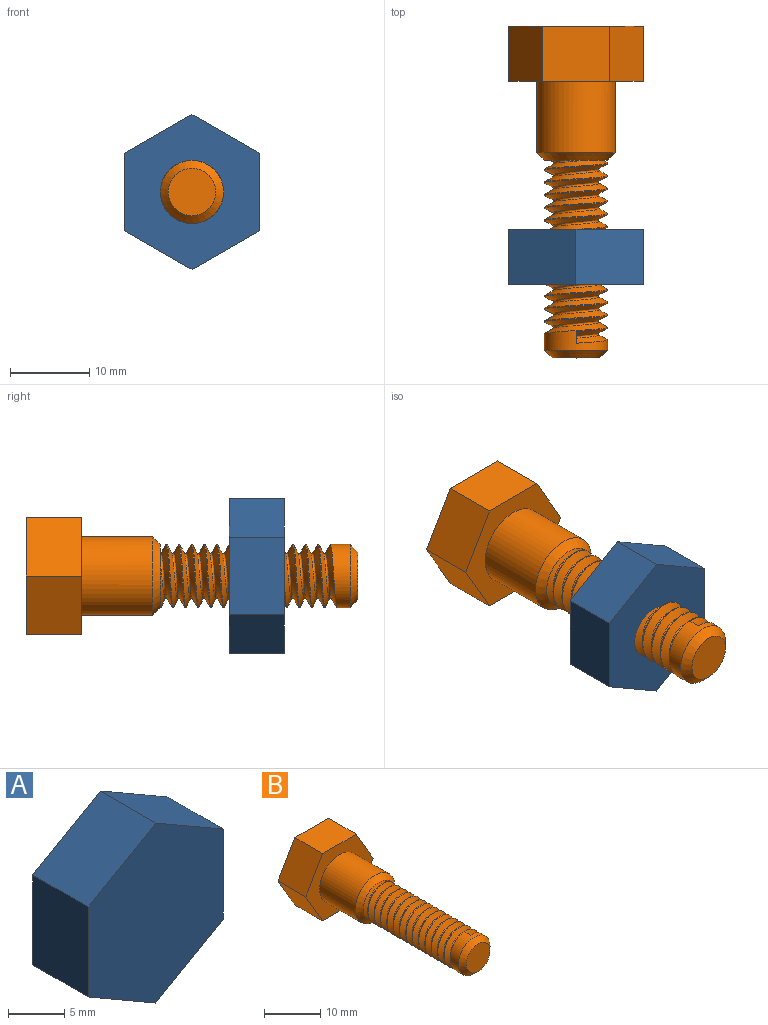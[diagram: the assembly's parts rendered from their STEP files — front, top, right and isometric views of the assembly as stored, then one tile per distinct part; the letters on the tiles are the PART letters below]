
ASSEMBLY  parts=2 mates=1
PART A: 8 faces, bbox 17x7x19.6 mm
  f0: plane 9.82x7mm, normal (1,0,0), area 68.7mm2, adj f1,f5,f6,f7
  f1: plane 8.5x7mm, normal (0.5,0,0.87), area 68.7mm2, adj f0,f2,f6,f7
  f2: plane 8.5x7mm, normal (-0.5,0,0.87), area 68.7mm2, adj f1,f3,f6,f7
  f3: plane 9.82x7mm, normal (-1,0,0), area 68.7mm2, adj f2,f4,f6,f7
  f4: plane 8.5x7mm, normal (-0.5,0,-0.87), area 68.7mm2, adj f3,f5,f6,f7
  f5: plane 8.5x7mm, normal (0.5,0,-0.87), area 68.7mm2, adj f0,f4,f6,f7
  f6: plane 19.63x17mm, normal (0,-1,0), area 250.3mm2, adj f0,f1,f2,f3,f4,f5
  f7: plane 19.63x17mm, normal (0,1,0), area 250.3mm2, adj f0,f1,f2,f3,f4,f5
PART B: 33 faces, bbox 17x42x14.7 mm
  f0: cylinder r=4mm len=8mm, axis (0,1,0), area 41.8mm2, adj f1,f26,f28,f32
  f1: cylinder r=4mm len=8mm, axis (0,1,0), area 2.5mm2, adj f0,f2,f30,f32
  f2: cylinder r=4mm len=8mm, axis (0,1,0), area 2.5mm2, adj f1,f3,f30,f32
  f3: cylinder r=4mm len=8mm, axis (0,1,0), area 2.5mm2, adj f2,f4,f30,f32
  f4: cylinder r=4mm len=8mm, axis (0,1,0), area 2.5mm2, adj f3,f5,f30,f32
  f5: cylinder r=4mm len=8mm, axis (0,1,0), area 2.5mm2, adj f4,f6,f30,f32
  f6: cylinder r=4mm len=8mm, axis (0,1,0), area 2.5mm2, adj f5,f7,f30,f32
  f7: cylinder r=4mm len=8mm, axis (0,1,0), area 2.5mm2, adj f6,f8,f30,f32
  f8: cylinder r=4mm len=8mm, axis (0,1,0), area 2.5mm2, adj f7,f9,f30,f32
  f9: cylinder r=4mm len=8mm, axis (0,1,0), area 2.5mm2, adj f8,f10,f30,f32
  f10: cylinder r=4mm len=8mm, axis (0,1,0), area 2.5mm2, adj f9,f11,f30,f32
  f11: cylinder r=4mm len=8mm, axis (0,1,0), area 2.5mm2, adj f10,f12,f30,f32
  f12: cylinder r=4mm len=8mm, axis (0,1,0), area 2.5mm2, adj f11,f13,f30,f32
  f13: cylinder r=4mm len=8mm, axis (0,1,0), area 2.5mm2, adj f12,f14,f30,f32
  f14: cylinder r=4mm len=8mm, axis (0,1,0), area 1.3mm2, adj f13,f25,f30,f32
  f15: plane 8.5x7mm, normal (0,0,1), area 59.5mm2, adj f16,f20,f21,f22
  f16: plane 7.36x7mm, normal (-0.87,0,0.5), area 59.5mm2, adj f15,f17,f21,f22
  f17: plane 7.36x7mm, normal (-0.87,0,-0.5), area 59.5mm2, adj f16,f18,f21,f22
  f18: plane 8.5x7mm, normal (0,0,-1), area 59.5mm2, adj f17,f19,f21,f22
  f19: plane 7.36x7mm, normal (0.87,0,-0.5), area 59.5mm2, adj f18,f20,f21,f22
  f20: plane 7.36x7mm, normal (0.87,0,0.5), area 59.5mm2, adj f15,f19,f21,f22
  f21: plane 17x14.72mm, normal (0,-1,0), area 109.2mm2, adj f15,f16,f17,f18,f19,f20,f23
  f22: plane 17x14.72mm, normal (0,1,0), area 187.7mm2, adj f15,f16,f17,f18,f19,f20
  f23: cylinder r=5mm len=10mm, axis (0,1,0), area 282.7mm2, adj f21,f25
  f24: plane 6x6mm, normal (0,-1,0), area 28.3mm2, adj f26
  f25: cone r=4mm half-angle=45deg, axis (0,1,0), area 40mm2, adj f14,f23,f29
  f26: cone r=3mm half-angle=45deg, axis (0,1,0), area 31.1mm2, adj f0,f24
  f27: plane 1.52x1.19mm, normal (-1,0,0), area 1mm2, adj f29,f30,f31,f32
  f28: plane 1.52x1.19mm, normal (1,0,0), area 1mm2, adj f0,f30,f31,f32
  f29: cylinder r=4mm len=8mm, axis (0,-1,0), area 38mm2, adj f25,f27,f30,f32
  f30: bspline ~24.53x9.24mm, area 387.5mm2, adj f1,f2,f3,f4,f5,f6,f7,f8
  f31: bspline ~24.35x6.79mm, area 116.2mm2, adj f27,f28,f30,f32
  f32: bspline ~24.62x9.24mm, area 404.7mm2, adj f0,f1,f2,f3,f4,f5,f6,f7
PLACE A t=(-25.52,-39.49,-42.4)mm
PLACE B t=(-25.52,-13.79,-7.19)mm fixed
MATE slider B.f0 <-> A.f7  axis (0,-1,0) through (-25.52,-55.79,-7.19)mm
